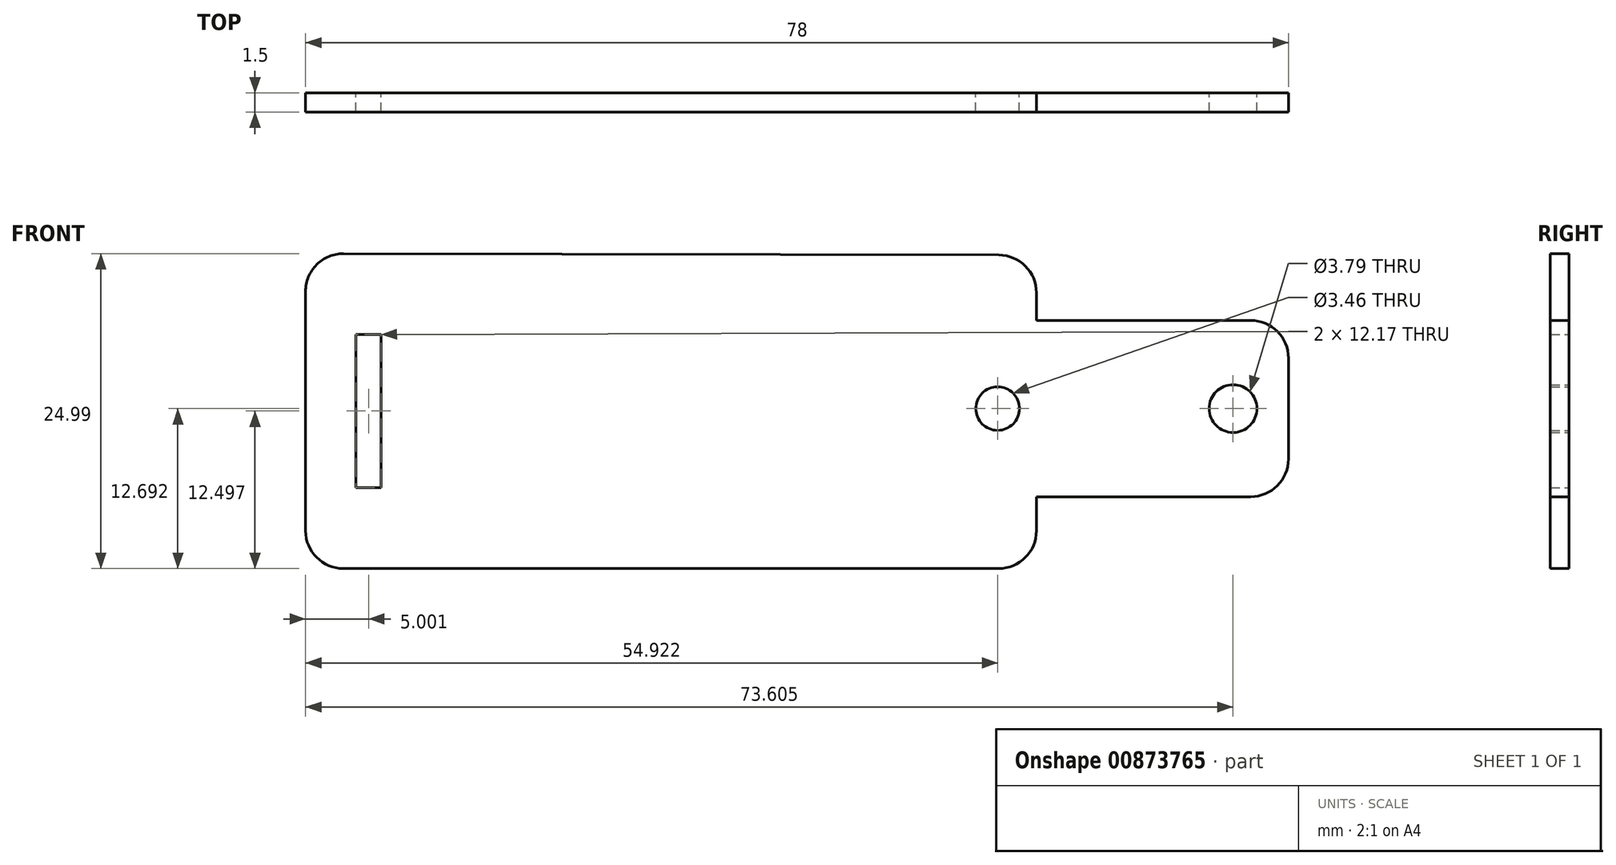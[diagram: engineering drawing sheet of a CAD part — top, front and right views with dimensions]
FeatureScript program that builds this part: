
annotation { "Feature Type Name" : "Feature", "Feature Type Description" : "" }
export const myFeature = defineFeature(function(context is Context, id is Id, definition is map)
    precondition{}
    {
        {
            var Q0;
            Q0=qCreatedBy(makeId("Front.planeOp"),FACE);
            var sketch = newSketch(context, id + "F0", { "sketchPlane" : qUnion([Q0])});
            skLineSegment(sketch, "E0", {"start": v(-36.95, 22) * mm, "end": v(-36.95, 3) * mm});
            skLineSegment(sketch, "E1", {"start": v(-33.95, 0) * mm, "end": v(18.05, 0) * mm});
            skLineSegment(sketch, "E2", {"start": v(21.05, 3) * mm, "end": v(21.05, 5.7) * mm});
            skLineSegment(sketch, "E3", {"start": v(21.05, 5.7) * mm, "end": v(38.05, 5.7) * mm});
            skLineSegment(sketch, "E4", {"start": v(41.05, 8.7) * mm, "end": v(41.05, 16.7) * mm});
            skLineSegment(sketch, "E5", {"start": v(38.05, 19.7) * mm, "end": v(21.05, 19.7) * mm});
            skLineSegment(sketch, "E6", {"start": v(21.05, 19.7) * mm, "end": v(21.05, 21.88) * mm});
            skLineSegment(sketch, "E7", {"start": v(18.06, 24.88) * mm, "end": v(-33.94, 25) * mm});
            skPoint(sketch, "E8.visualSharp", {"position": v(-36.95, 25) * mm});
            skArc(sketch, "E8.filletArc", {"start": v(-33.94, 25) * mm, "mid": v(-36.07, 24.12) * mm, "end": v(-36.95, 22) * mm});
            skPoint(sketch, "E9.visualSharp", {"position": v(-36.95, 0) * mm});
            skArc(sketch, "E9.filletArc", {"start": v(-36.95, 3) * mm, "mid": v(-36.07, 0.88) * mm, "end": v(-33.95, 0) * mm});
            skPoint(sketch, "E10.visualSharp", {"position": v(21.05, 24.88) * mm});
            skArc(sketch, "E10.filletArc", {"start": v(21.05, 21.88) * mm, "mid": v(20.17, 24) * mm, "end": v(18.06, 24.88) * mm});
            skPoint(sketch, "E11.visualSharp", {"position": v(21.05, 0) * mm});
            skArc(sketch, "E11.filletArc", {"start": v(18.05, 0) * mm, "mid": v(20.17, 0.88) * mm, "end": v(21.05, 3) * mm});
            skPoint(sketch, "E12.visualSharp", {"position": v(41.05, 19.7) * mm});
            skArc(sketch, "E12.filletArc", {"start": v(41.05, 16.7) * mm, "mid": v(40.17, 18.81) * mm, "end": v(38.05, 19.7) * mm});
            skPoint(sketch, "E13.visualSharp", {"position": v(41.05, 5.7) * mm});
            skArc(sketch, "E13.filletArc", {"start": v(38.05, 5.7) * mm, "mid": v(40.17, 6.57) * mm, "end": v(41.05, 8.7) * mm});
            skLineSegment(sketch, "E14", {"start": v(-36.95, 12.5) * mm, "end": v(-31.95, 12.5) * mm});
            skLineSegment(sketch, "E15.bottom", {"start": v(-30.95, 18.58) * mm, "end": v(-32.95, 18.58) * mm});
            skLineSegment(sketch, "E15.top", {"start": v(-30.95, 6.41) * mm, "end": v(-32.95, 6.41) * mm});
            skLineSegment(sketch, "E15.left", {"start": v(-30.95, 18.58) * mm, "end": v(-30.95, 6.41) * mm});
            skLineSegment(sketch, "E15.right", {"start": v(-32.95, 18.58) * mm, "end": v(-32.95, 6.41) * mm});
            skPoint(sketch, "E15.middle", {"position": v(-31.95, 12.5) * mm});
            skCircle(sketch, "E16", {"center": v(36.66, 12.7) * mm, "radius": 1.9 * mm});
            skPoint(sketch, "E16.centerSnap0", {"position": v(41.05, 12.7) * mm});
            skCircle(sketch, "E17", {"center": v(17.97, 12.7) * mm, "radius": 1.73 * mm});
            skLineSegment(sketch, "E18", {"start": v(36.66, 12.7) * mm, "end": v(36.66, 14.59) * mm, "construction": true});
            skLineSegment(sketch, "E19", {"start": v(17.97, 12.7) * mm, "end": v(17.98, 14.42) * mm, "construction": true});
            skPoint(sketch, "E20.orphan", {"position": v(18.05, 33.08) * mm});
            skLineSegment(sketch, "E21", {"start": v(38.55, 12.7) * mm, "end": v(38.55, 19.3) * mm, "construction": true});
            skLineSegment(sketch, "E22", {"start": v(19.7, 12.7) * mm, "end": v(19.7, 26.9) * mm, "construction": true});
            skSolve(sketch);
        }
        {
            var Q0;
            Q0=makeQuery(id+"F0.imprint","IMPRINT",FACE,{"disambiguationData":[TD([[makeQuery(id+"F0.imprint","IMPRINT",EDGE,{"derivedFrom":sQuery(id+"F0.wireOp",EDGE,"E1")}),1.0]])]});
            extrude(context, id + "F1", {"entities" : qUnion([Q0]), "depth" : 1.5 * mm, "offsetDistance" : 25 * mm});
        }
    });
